# Revit family: Building-Materials_Glass-Glazing_Vitro-Architectural-Glass_SOLARBAN-Acuity-Series
name_source: partatom
category: Curtain Panels
units: mm (PartAtom-declared; Revit-internal decimal feet)

## family parameters
Always vertical = Yes
Classification Number = 23.25.20.14.11.11.17
Cut with Voids When Loaded = No
Shared = No

## types (1)
- Acuity + Acuity
    1st Lite Thickness = 0' - 0 1/4"
    2nd Lite Thickness = 0' - 0 1/4"
    Airspace Thickness = 0' - 0 1/2"
    Analytic Construction = Low-E double glazing (1/4 in + 1/4 in)
    Assembly Code = B2020220
    Define Thermal Properties by = Schematic Type
    Description = The right glass can be the centerpiece of your design. Combining the color fidelity of new Acuity™ low‑iron glass with the performance you expect from the Solarban® family of glasses, you can design an ambitious facade-and actually realize it, on budget and on time. Acuity™ glass is available with the full range of Solarban® solar control, low‑e coatings.
    Exterior Glass Material = Vitro Architectural-Glass - Acuity
    Finish = Glass
    Glass Code = 3
    Heat Transfer Coefficient (U) = 0.29 BTU/(h·ft²·°F)
    ISO Damage Weighted Transmittance = 0.764
    Interior Glass Material = Vitro Architectural-Glass - Acuity
    Keynote = 08900
    Light to Solar Gain = 1.05
    Manufacturer = Vitro Architectural Glass
    Model = Acuity + Acuity
    Product Guid = a7815d87-3680-4471-99e1-be6fcc4030d8
    Product Page URL = https://www.vitroglazings.com
    Product data url = https://www.bimobject.com
    Reflectance (Visible Exterior) = 15
    Reflectance (Visible Interior) = 15
    Shadow Coefficient = 0.9
    Solar Heat Gain Coefficient = 0.78
    Solar Light Transmittance = 0.73
    Thermal Resistance (R) = 8.3333 (h·ft²·°F)/BTU
    Total Thickness = 0' - 1"
    U-Value Air (Summer Day) = 0.5 BTU/(h·ft²·°F)
    U-Value Air (Winter Night) = 0.47 BTU/(h·ft²·°F)
    U-Value Argon (Summer Day) = 0.48 BTU/(h·ft²·°F)
    U-Value Argon (Winter Night) = 0.45 BTU/(h·ft²·°F)
    URL = https://www.vitroglazings.com
    UV Light Transmittance = 0.63
    Visual Light Transmittance = 0.82

## geometry (parser evidence)
native form markers: Sweep x2
no freeform markers — native parametric forms only
